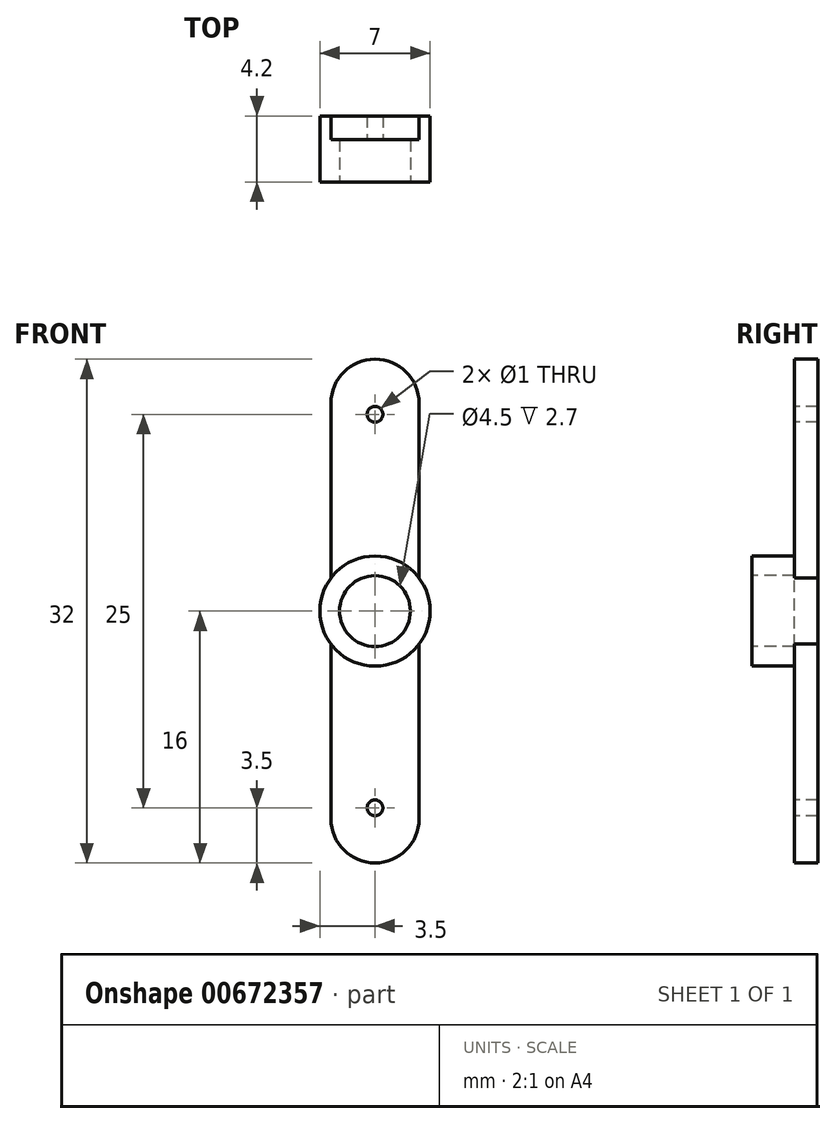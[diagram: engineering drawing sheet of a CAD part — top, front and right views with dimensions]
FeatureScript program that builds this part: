
annotation { "Feature Type Name" : "Feature", "Feature Type Description" : "" }
export const myFeature = defineFeature(function(context is Context, id is Id, definition is map)
    precondition{}
    {
        {
            var Q0;
            Q0=qCreatedBy(makeId("Front.planeOp"),FACE);
            var sketch = newSketch(context, id + "F0", { "sketchPlane" : qUnion([Q0])});
            skCircle(sketch, "E0", {"center": v(0, 0) * mm, "radius": 3.5 * mm});
            skSolve(sketch);
        }
        {
            var Q0;
            Q0 = qSketchRegion(id + "F0", true);
            extrude(context, id + "F1", {"entities" : qUnion([Q0]), "oppositeDirection" : true, "depth" : 4.2 * mm, "offsetDistance" : 25 * mm});
        }
        {
            var Q0;
            Q0=makeQuery(id+"F1.opExtrude","CAP_FACE",FACE,{"disambiguationData":[OSD([sQuery(id+"F0.wireOp",EDGE,"E0")])],"isStart":false});
            var sketch = newSketch(context, id + "F2", { "sketchPlane" : qUnion([Q0])});
            skLineSegment(sketch, "E1.left", {"start": v(-2.8, 13.2) * mm, "end": v(-2.8, -13.2) * mm});
            skLineSegment(sketch, "E1.right", {"start": v(2.8, 13.2) * mm, "end": v(2.8, -13.2) * mm});
            skArc(sketch, "E2", {"start": v(2.8, 13.2) * mm, "mid": v(0, 16) * mm, "end": v(-2.8, 13.2) * mm});
            skArc(sketch, "E3", {"start": v(-2.8, -13.2) * mm, "mid": v(0, -16) * mm, "end": v(2.8, -13.2) * mm});
            skPoint(sketch, "E4.orphan", {"position": v(-2.8, 16) * mm});
            skPoint(sketch, "E5.orphan", {"position": v(2.8, 16) * mm});
            skPoint(sketch, "E6.orphan", {"position": v(-2.8, -16) * mm});
            skSolve(sketch);
        }
        {
            var Q0;
            Q0 = qSketchRegion(id + "F2", true);
            extrude(context, id + "F3", {"entities" : qUnion([Q0]), "operationType" : NewBodyOperationType.ADD, "oppositeDirection" : true, "depth" : 1.5 * mm, "offsetDistance" : 25 * mm});
        }
        {
            var Q0;
            {var subQ0=sQuery(id+"F2.wireOp",EDGE,"E1.left");var subQ1=sQuery(id+"F2.wireOp",EDGE,"E1.right");var subQ2=sQuery(id+"F2.wireOp",EDGE,"E2");Q0=makeQuery(id+"F3.boolean.opBoolean","SPLIT",FACE,{"disambiguationData":[TD([makeQuery(id+"F3.opExtrude","SWEPT_FACE",FACE,{"disambiguationData":[OSD([subQ2])]})])],"derivedFrom":makeQuery(id+"F3.opExtrude","CAP_FACE",FACE,{"disambiguationData":[OSD([subQ0,subQ1,subQ2,sQuery(id+"F2.wireOp",EDGE,"E3")])],"isStart":false})});}
            var sketch = newSketch(context, id + "F4", { "sketchPlane" : qUnion([Q0])});
            skCircle(sketch, "E7", {"center": v(0, 12.5) * mm, "radius": 0.5 * mm});
            skCircle(sketch, "E8", {"center": v(0, -12.5) * mm, "radius": 0.5 * mm});
            skSolve(sketch);
        }
        {
            var Q0;
            Q0 = qSketchRegion(id + "F4", true);
            extrude(context, id + "F5", {"entities" : qUnion([Q0]), "operationType" : NewBodyOperationType.REMOVE, "oppositeDirection" : true, "depth" : 25 * mm, "offsetDistance" : 25 * mm});
        }
        {
            var Q0;
            Q0=makeQuery(id+"F1.opExtrude","CAP_FACE",FACE,{"disambiguationData":[OSD([sQuery(id+"F0.wireOp",EDGE,"E0")])],"isStart":true});
            var sketch = newSketch(context, id + "F6", { "sketchPlane" : qUnion([Q0])});
            skCircle(sketch, "E9", {"center": v(0, 0) * mm, "radius": 2.25 * mm});
            skSolve(sketch);
        }
        {
            var Q0;
            Q0 = qSketchRegion(id + "F6", true);
            extrude(context, id + "F7", {"entities" : qUnion([Q0]), "operationType" : NewBodyOperationType.REMOVE, "oppositeDirection" : true, "depth" : 2.7 * mm, "offsetDistance" : 25 * mm});
        }
    });
